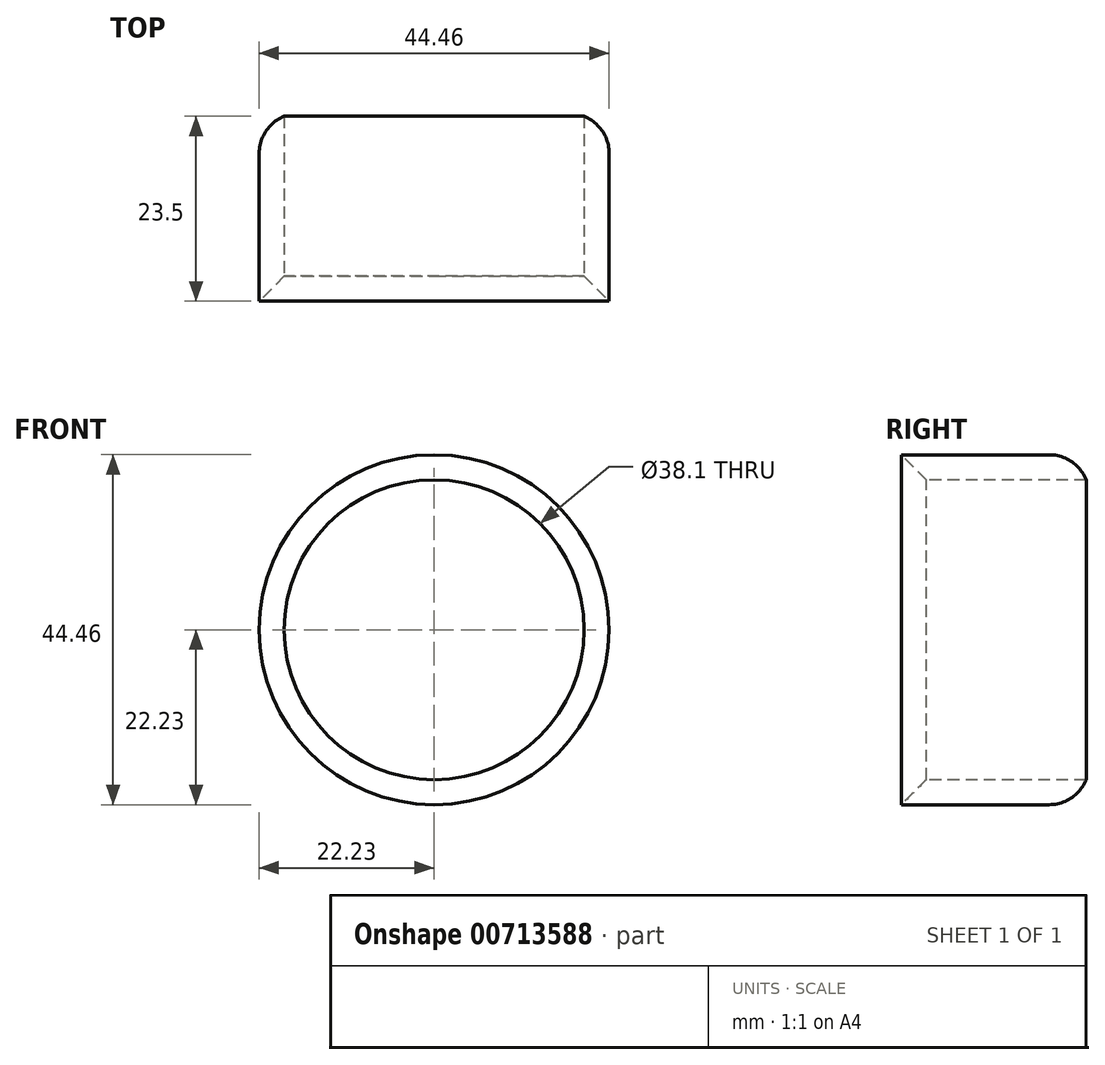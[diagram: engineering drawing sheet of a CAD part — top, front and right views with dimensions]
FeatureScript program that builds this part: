
annotation { "Feature Type Name" : "Feature", "Feature Type Description" : "" }
export const myFeature = defineFeature(function(context is Context, id is Id, definition is map)
    precondition{}
    {
        {
            var Q0;
            Q0=qCreatedBy(makeId("Front.planeOp"),FACE);
            var sketch = newSketch(context, id + "F0", { "sketchPlane" : qUnion([Q0])});
            skCircle(sketch, "E0", {"center": v(0, 0) * mm, "radius": 22.23 * mm});
            skSolve(sketch);
        }
        {
            var Q0;
            Q0 = qSketchRegion(id + "F0", true);
            extrude(context, id + "F1", {"entities" : qUnion([Q0]), "oppositeDirection" : true, "depth" : 25.4 * mm, "offsetDistance" : 25.4 * mm});
        }
        {
            var Q0;
            Q0=makeQuery(id+"F1.opExtrude","CAP_FACE",FACE,{"disambiguationData":[OSD([sQuery(id+"F0.wireOp",EDGE,"E0")])],"isStart":true});
            var Q1;
            Q1=makeQuery(id+"F1.opExtrude","CAP_FACE",FACE,{"disambiguationData":[OSD([sQuery(id+"F0.wireOp",EDGE,"E0")])],"isStart":false});
            var Q2;
            Q2=makeQuery(id+"F1.opExtrude","SWEPT_BODY",BODY,{"disambiguationData":[OSD([sQuery(id+"F0.wireOp",EDGE,"E0")])]});
            shell(context, id + "F2", {"entities" : qUnion([Q0, Q1]), "parts" : qUnion([Q2]), "thickness" : 3.17 * mm});
        }
        {
            var Q0;
            {var subQ0=sQuery(id+"F0.wireOp",EDGE,"E0");Q0=makeQuery(id+"F2.opShell","OFFSET_EDGE",EDGE,{"disambiguationData":[OSD([subQ0]),TDD([makeQuery(id+"F1.opExtrude","CAP_EDGE",EDGE,{"disambiguationData":[OSD([subQ0])],"isStart":true})])]});}
            chamfer(context, id + "F3", {"entities" : qUnion([Q0]), "width" : 5.08 * mm, "tangentPropagation" : true});
        }
        {
            var Q0;
            Q0=makeQuery(id+"F1.opExtrude","CAP_EDGE",EDGE,{"disambiguationData":[OSD([sQuery(id+"F0.wireOp",EDGE,"E0")])],"isStart":false});
            fillet(context, id + "F4", {"entities" : qUnion([Q0]), "radius" : 5.08 * mm, "tangentPropagation" : true, "allowEdgeOverflow" : false});
        }
    });
